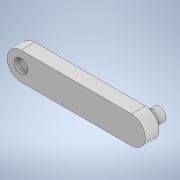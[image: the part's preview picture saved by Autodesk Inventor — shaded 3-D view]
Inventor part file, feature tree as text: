
AUTODESK INVENTOR PART (.ipt)
format: ipt  version: 2022 (Build 260153000, 153)  size: 108,032 bytes
history: native  units: mm
features: extrude x2, sketch x1
ambient origin geometry x8: Origin, YZ Plane, XZ Plane, XY Plane, X Axis, Y Axis, Z Axis, Center Point
bodies: Solid1 (feature_tree)
feature tree (3):
  sketch  "Sketch1"  dims[d0=40.0mm d1=10.0mm d2=5.0mm d3=5.0mm d4=0.0mm d5=5.0mm d6=0.0mm]
  extrude  "Extrusion1"  Depth=10.0mm
  extrude  "Extrusion2"  Depth=5.0mm
